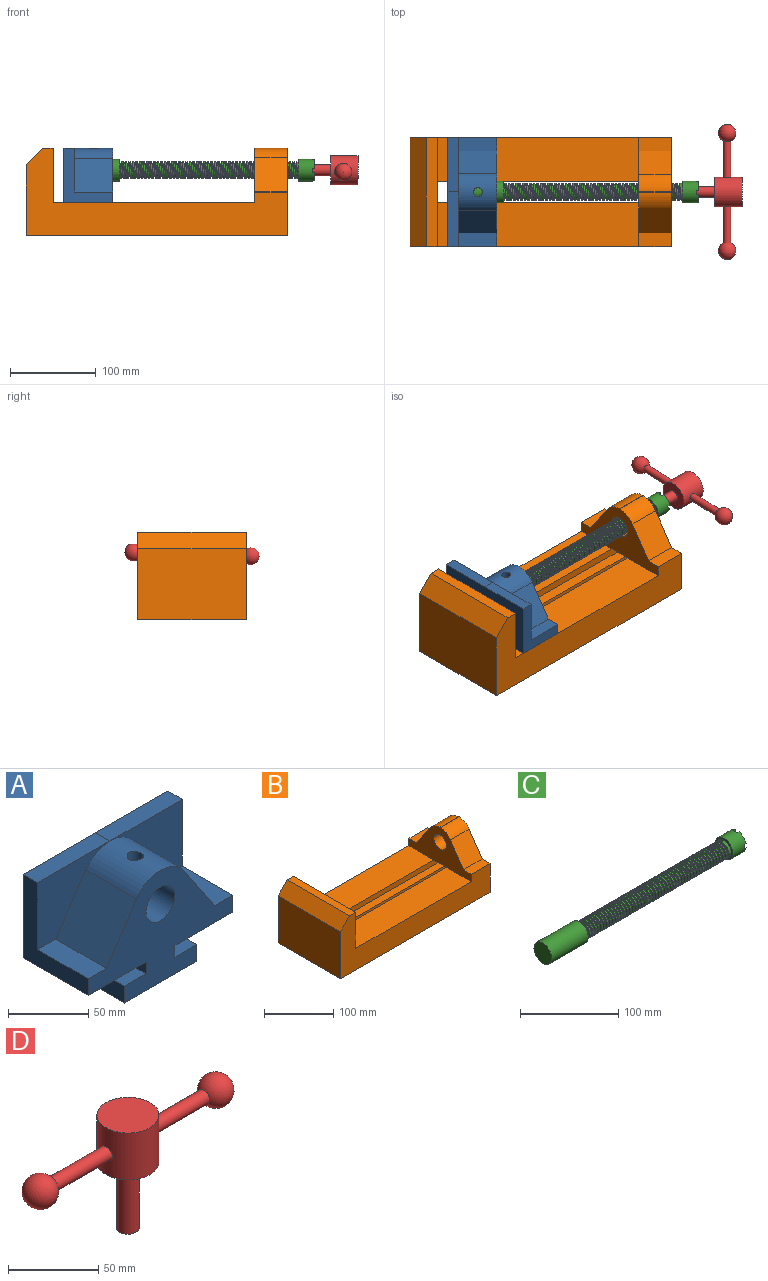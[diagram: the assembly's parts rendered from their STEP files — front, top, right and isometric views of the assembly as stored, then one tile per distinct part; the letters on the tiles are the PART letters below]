
ASSEMBLY  parts=4 mates=3
PART A: 26 faces, bbox 127x57.2x85.1 mm
  f0: cylinder r=12.7mm len=44.45mm, axis (0,1,0), area 3464.2mm2, adj f17,f24,f25
  f1: plane 44.45x12.7mm, normal (1,0,0), area 564.5mm2, adj f2,f16,f17,f18
  f2: plane 44.45x19.05mm, normal (0,0,1), area 846.8mm2, adj f1,f3,f17,f18
  f3: plane 44.45x8.89mm, normal (1,0,0), area 395.2mm2, adj f2,f11,f17,f18
  f4: plane 63.5x57.15mm, normal (1,0,0), area 1371mm2, adj f5,f11,f17,f19,f20,f22
  f5: plane 44.45x15.88mm, normal (0,0,1), area 705.6mm2, adj f4,f6,f17,f22
  f6: plane 44.45x39.55mm, normal (0.83,0,0.56), area 2116.9mm2, adj f5,f7,f17,f22
  f7: cylinder r=25.4mm len=44.45mm, axis (0,1,0), area 2131.3mm2, adj f6,f8,f17,f22,f23,f25
  f8: plane 44.45x39.55mm, normal (-0.83,0,0.56), area 2116.9mm2, adj f7,f9,f17,f23
  f9: plane 44.45x15.88mm, normal (0,0,1), area 705.6mm2, adj f8,f10,f17,f23
  f10: plane 63.5x57.15mm, normal (-1,0,0), area 1371mm2, adj f9,f11,f17,f19,f21,f23
  f11: plane 127x57.15mm, normal (0,0,-1), area 6129mm2, adj f3,f4,f10,f12,f17,f18,f19
  f12: plane 44.45x8.89mm, normal (-1,0,0), area 395.2mm2, adj f11,f13,f17,f18
  f13: plane 44.45x19.05mm, normal (0,0,1), area 846.8mm2, adj f12,f14,f17,f18
  f14: plane 44.45x12.7mm, normal (-1,0,0), area 564.5mm2, adj f13,f15,f17,f18
  f15: plane 44.45x31.75mm, normal (0,0,-1), area 1411.3mm2, adj f14,f16,f17,f18
  f16: plane 44.45x31.75mm, normal (0,0,-1), area 1411.3mm2, adj f1,f15,f17,f18
  f17: plane 127x85.09mm, normal (0,-1,0), area 5190mm2, adj f0,f1,f2,f3,f4,f5,f6,f7
  f18: plane 63.5x21.59mm, normal (0,1,0), area 1032.3mm2, adj f1,f2,f3,f11,f12,f13,f14,f15
  f19: plane 127x63.5mm, normal (0,1,0), area 8064.5mm2, adj f4,f10,f11,f20,f21
  f20: plane 63.5x12.7mm, normal (0,0,1), area 806.5mm2, adj f4,f19,f21,f22
  f21: plane 63.5x12.7mm, normal (0,0,1), area 806.5mm2, adj f10,f19,f20,f23
  f22: plane 63.5x50.8mm, normal (0,-1,0), area 1700mm2, adj f4,f5,f6,f7,f20
  f23: plane 63.5x50.8mm, normal (0,-1,0), area 1700mm2, adj f7,f8,f9,f10,f21
  f24: plane 25.4x25.4mm, normal (0,-1,0), area 506.7mm2, adj f0
  f25: cylinder r=5.08mm len=13.76mm, axis (0,0,1), area 414mm2, adj f0,f7
PART B: 30 faces, bbox 304.8x127x101.6 mm
  f0: plane 234.95x50.8mm, normal (0,0,1), area 11935.5mm2, adj f2,f6,f10,f24
  f1: plane 38.11x0.75mm, normal (0,0,1), area 28.4mm2, adj f2,f4,f12,f15
  f2: plane 127x63.5mm, normal (-1,0,0), area 4167.8mm2, adj f0,f1,f5,f9,f10,f12,f13,f14
  f3: plane 304.8x127mm, normal (0,0,-1), area 31774.1mm2, adj f4,f6,f8,f9,f10,f19,f20
  f4: plane 127x101.6mm, normal (1,0,0), area 7554.9mm2, adj f1,f3,f9,f10,f12,f13,f14,f15
  f5: plane 234.95x50.8mm, normal (0,0,1), area 11935.5mm2, adj f2,f6,f9,f26
  f6: plane 127x101.6mm, normal (1,0,0), area 9516.1mm2, adj f0,f3,f5,f7,f9,f10,f18,f19
  f7: plane 127x12.7mm, normal (0,0,1), area 1612.9mm2, adj f6,f9,f10,f11
  f8: plane 127x82.55mm, normal (-1,0,0), area 10483.8mm2, adj f3,f9,f10,f11
  f9: plane 304.8x101.6mm, normal (0,-1,0), area 13931.4mm2, adj f2,f3,f4,f5,f6,f7,f8,f11
  f10: plane 304.8x101.6mm, normal (0,1,0), area 13931.4mm2, adj f0,f2,f3,f4,f6,f7,f8,f11
  f11: plane 127x19.05mm, normal (-0.71,0,0.71), area 3421.5mm2, adj f7,f8,f9,f10
  f12: cylinder r=25.4mm len=38.1mm, axis (1,0,0), area 900mm2, adj f1,f2,f4,f13
  f13: plane 40.28x38.1mm, normal (0,0.83,0.56), area 1848.6mm2, adj f2,f4,f12,f14
  f14: plane 38.1x15.88mm, normal (0,0,1), area 604.8mm2, adj f2,f4,f10,f13
  f15: cylinder r=25.4mm len=38.1mm, axis (1,0,0), area 928.5mm2, adj f1,f2,f4,f17
  f16: plane 38.1x15.87mm, normal (0,-0.03,1), area 604.8mm2, adj f2,f4,f9,f17
  f17: plane 39.19x38.1mm, normal (0,-0.83,0.56), area 1805mm2, adj f2,f4,f15,f16
  f18: plane 273.05x19.05mm, normal (0,0,1), area 5201.6mm2, adj f4,f6,f19,f28
  f19: plane 273.05x16.51mm, normal (0,1,0), area 4508.1mm2, adj f3,f4,f6,f18
  f20: plane 273.05x16.51mm, normal (0,-1,0), area 4508.1mm2, adj f3,f4,f6,f21
  f21: plane 273.05x19.05mm, normal (0,0,1), area 5201.6mm2, adj f4,f6,f20,f22
  f22: plane 273.05x12.7mm, normal (0,-1,0), area 3467.7mm2, adj f4,f6,f21,f23
  f23: plane 273.05x19.05mm, normal (0,0,-1), area 5201.6mm2, adj f4,f6,f22,f24
  f24: plane 273.05x8.89mm, normal (0,-1,0), area 2427.4mm2, adj f0,f4,f6,f23,f25
  f25: plane 38.1x25.4mm, normal (0,0,-1), area 967.7mm2, adj f2,f4,f24,f26
  f26: plane 273.05x8.89mm, normal (0,1,0), area 2427.4mm2, adj f4,f5,f6,f25,f27
  f27: plane 273.05x19.05mm, normal (0,0,-1), area 5201.6mm2, adj f4,f6,f26,f28
  f28: plane 273.05x12.7mm, normal (0,1,0), area 3467.7mm2, adj f4,f6,f18,f27
  f29: cylinder r=12.7mm len=38.1mm, axis (1,0,0), area 3040.2mm2, adj f2,f4
PART C: 31 faces, bbox 279.4x25.4x25.4 mm
  f0: cylinder r=10.16mm len=207.9mm, axis (-1,0,0), area -543.2mm2, adj f6,f7,f25,f26,f28,f30
  f1: plane 9.9x9.9mm, normal (1,0,0), area 62.3mm2, adj f5,f16,f19,f22
  f2: plane 9.9x9.9mm, normal (1,0,0), area 62.3mm2, adj f5,f11,f20,f22
  f3: plane 9.9x9.9mm, normal (1,0,0), area 62.3mm2, adj f5,f10,f14,f22
  f4: plane 9.9x9.9mm, normal (1,0,0), area 62.3mm2, adj f5,f13,f17,f22
  f5: cylinder r=12.7mm len=25.4mm, axis (-1,0,0), area 1468.2mm2, adj f1,f2,f3,f4,f6,f10,f11,f12
  f6: plane 25.4x25.4mm, normal (-1,0,0), area 182.4mm2, adj f0,f5,f29
  f7: plane 25.4x25.4mm, normal (1,0,0), area 182.4mm2, adj f0,f8,f24
  f8: cylinder r=12.7mm len=52.45mm, axis (-1,0,0), area 4185.4mm2, adj f7,f9
  f9: plane 25.4x25.4mm, normal (-1,0,0), area 506.7mm2, adj f8
  f10: plane 6.62x2.54mm, normal (0,0,1), area 16.8mm2, adj f3,f5,f12,f22
  f11: plane 6.62x2.54mm, normal (0,0,-1), area 16.8mm2, adj f2,f5,f12,f22
  f12: plane 6.88x5.08mm, normal (1,0,0), area 32.7mm2, adj f5,f10,f11,f22
  f13: plane 6.62x2.54mm, normal (0,-1,0), area 16.8mm2, adj f4,f5,f15,f22
  f14: plane 6.62x2.54mm, normal (0,1,0), area 16.8mm2, adj f3,f5,f15,f22
  f15: plane 6.88x5.08mm, normal (1,0,0), area 32.7mm2, adj f5,f13,f14,f22
  f16: plane 6.62x2.54mm, normal (0,0,-1), area 16.8mm2, adj f1,f5,f18,f22
  f17: plane 6.62x2.54mm, normal (0,0,1), area 16.8mm2, adj f4,f5,f18,f22
  f18: plane 6.88x5.08mm, normal (1,0,0), area 32.7mm2, adj f5,f16,f17,f22
  f19: plane 6.62x2.54mm, normal (0,-1,0), area 16.8mm2, adj f1,f5,f21,f22
  f20: plane 6.62x2.54mm, normal (0,1,0), area 16.8mm2, adj f2,f5,f21,f22
  f21: plane 6.88x5.08mm, normal (1,0,0), area 32.7mm2, adj f5,f19,f20,f22
  f22: cylinder r=6.35mm len=25.4mm, axis (1,0,0), area 960.3mm2, adj f1,f2,f3,f4,f10,f11,f12,f13
  f23: plane 12.7x12.7mm, normal (1,0,0), area 126.7mm2, adj f22
  f24: cylinder r=10.16mm len=20.32mm, axis (1,0,0), area 47.7mm2, adj f7,f25,f30
  f25: plane 2.54x2mm, normal (0,-1,0), area 4.2mm2, adj f0,f24,f27,f28,f30
  f26: plane 2.54x2mm, normal (0,1,0), area 4.2mm2, adj f0,f27,f28,f29,f30
  f27: cylinder r=8.16mm len=209.52mm, axis (1,0,0), area 4143mm2, adj f25,f26,f28,f30
  f28: bspline ~208.36x23.46mm, area 5955.7mm2, adj f0,f25,f26,f27,f29
  f29: cylinder r=10.16mm len=0.79mm, axis (1,0,0), area 0mm2, adj f6,f26,f28
  f30: bspline ~208.36x23.46mm, area 5955.4mm2, adj f0,f24,f25,f26,f27
PART D: 9 faces, bbox 157.6x34.3x76.2 mm
  f0: cylinder r=17.16mm len=34.32mm, axis (0,0,1), area 3297.7mm2, adj f1,f2,f5,f7
  f1: plane 34.32x34.32mm, normal (0,0,-1), area 798.2mm2, adj f0,f3
  f2: plane 34.32x34.32mm, normal (0,0,1), area 924.9mm2, adj f0
  f3: cylinder r=6.35mm len=44.45mm, axis (0,0,1), area 1773.5mm2, adj f1,f4
  f4: plane 12.7x12.7mm, normal (0,0,-1), area 126.7mm2, adj f3
  f5: cylinder r=4.45mm len=42.92mm, axis (1,0,0), area 1190.5mm2, adj f0,f6
  f6: sphere r=10.16mm, area 1231.8mm2, adj f5
  f7: cylinder r=4.45mm len=42.92mm, axis (1,0,0), area 1190.5mm2, adj f0,f8
  f8: sphere r=10.16mm, area 1231.8mm2, adj f7
PLACE A rot(axis=(0,0,1),90deg) t=(57.01,-63.5,38.1)mm
PLACE B at identity fixed
PLACE C rot(axis=(-1,0,0),178.1deg) t=(57.01,-63.5,76.2)mm
PLACE D rot(axis=(0.58,0.56,0.58),121.1deg) t=(355.46,-63.5,76.2)mm
MATE fastened C.f0 <-> D.f0  axis (1,0,0) through (311.01,-63.5,76.2)mm
MATE revolute A.f0 <-> C.f0  axis (-1,0,0) through (57.01,-63.5,76.2)mm
MATE slider B.f6 <-> A.f19  axis (1,0,0) through (31.75,-127,38.1)mm
